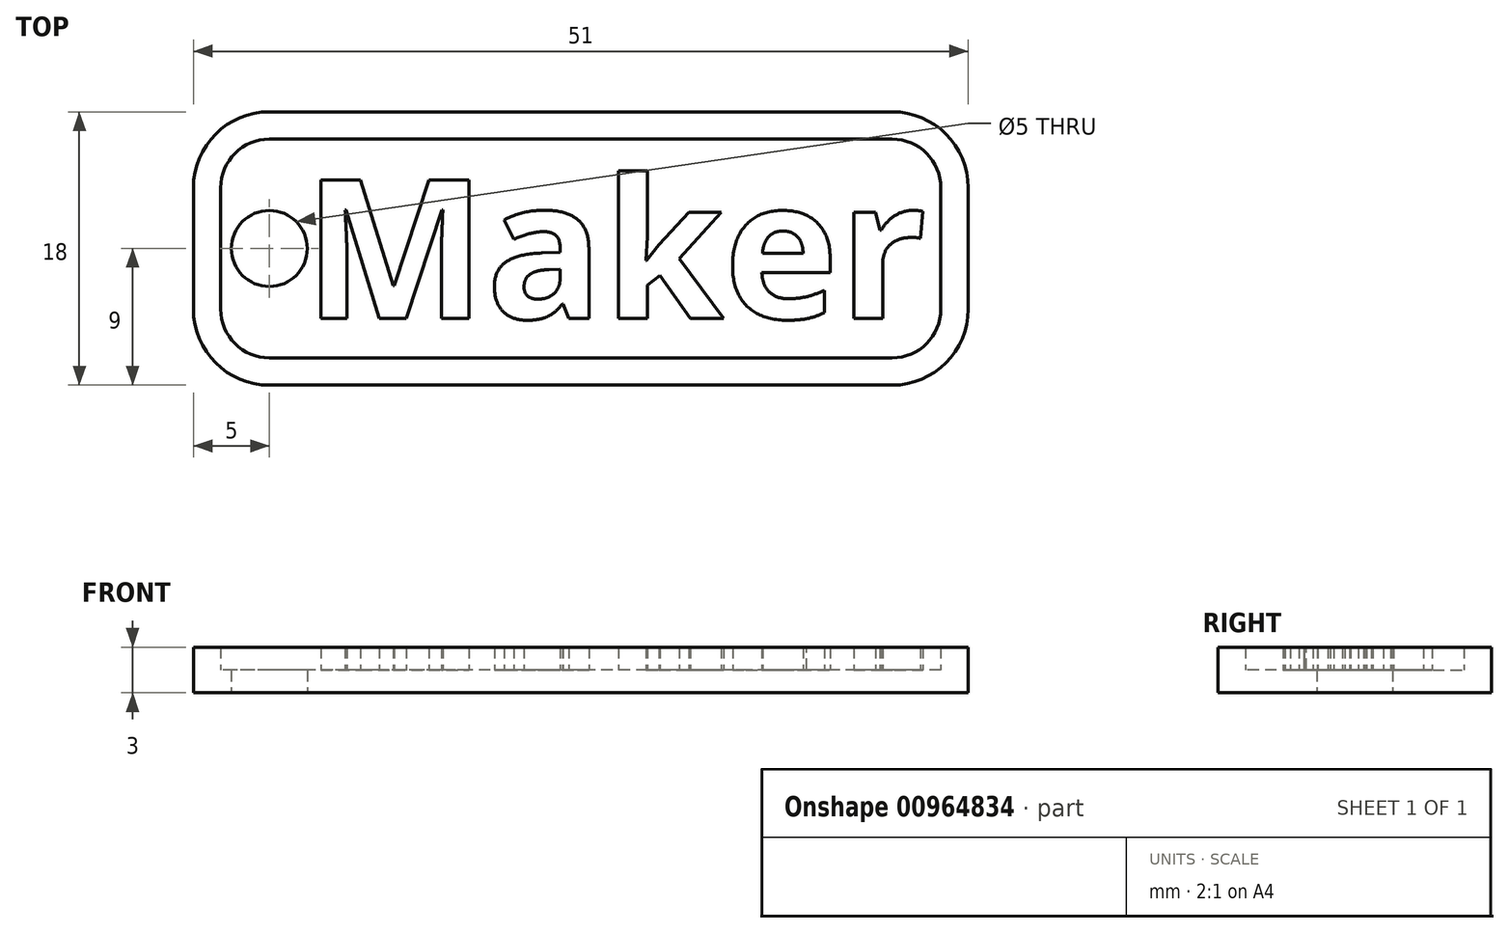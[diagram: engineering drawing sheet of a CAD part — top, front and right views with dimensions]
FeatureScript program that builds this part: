
annotation { "Feature Type Name" : "Feature", "Feature Type Description" : "" }
export const myFeature = defineFeature(function(context is Context, id is Id, definition is map)
    precondition{}
    {
        {
            var Q0;
            Q0=qCreatedBy(makeId("Top.planeOp"),FACE);
            var sketch = newSketch(context, id + "F0", { "sketchPlane" : qUnion([Q0])});
            skLineSegment(sketch, "E0.bottom", {"start": v(5, 0) * mm, "end": v(46, 0) * mm});
            skLineSegment(sketch, "E0.top", {"start": v(5, 18) * mm, "end": v(46, 18) * mm});
            skLineSegment(sketch, "E0.left", {"start": v(0, 5) * mm, "end": v(0, 13) * mm});
            skLineSegment(sketch, "E0.right", {"start": v(51, 5) * mm, "end": v(51, 13) * mm});
            skPoint(sketch, "E1.visualSharp", {"position": v(0, 18) * mm});
            skArc(sketch, "E1.filletArc", {"start": v(5, 18) * mm, "mid": v(1.46, 16.54) * mm, "end": v(0, 13) * mm});
            skPoint(sketch, "E2.visualSharp", {"position": v(0, 0) * mm});
            skArc(sketch, "E2.filletArc", {"start": v(0, 5) * mm, "mid": v(1.46, 1.46) * mm, "end": v(5, 0) * mm});
            skPoint(sketch, "E3.visualSharp", {"position": v(51, 0) * mm});
            skArc(sketch, "E3.filletArc", {"start": v(46, 0) * mm, "mid": v(49.54, 1.46) * mm, "end": v(51, 5) * mm});
            skPoint(sketch, "E4.visualSharp", {"position": v(51, 18) * mm});
            skArc(sketch, "E4.filletArc", {"start": v(51, 13) * mm, "mid": v(49.54, 16.54) * mm, "end": v(46, 18) * mm});
            skCircle(sketch, "E5", {"center": v(5, 9) * mm, "radius": 2.5 * mm});
            skSolve(sketch);
        }
        {
            var Q0;
            Q0=makeQuery(id+"F0.imprint","IMPRINT",FACE,{"disambiguationData":[TD([[makeQuery(id+"F0.imprint","IMPRINT",EDGE,{"derivedFrom":sQuery(id+"F0.wireOp",EDGE,"E0.bottom")}),1.0]])]});
            extrude(context, id + "F1", {"entities" : qUnion([Q0]), "depth" : 1.5 * mm, "offsetDistance" : 25 * mm});
        }
        {
            var Q0;
            Q0=makeQuery(id+"F1.opExtrude","CAP_FACE",FACE,{"disambiguationData":[OSD([sQuery(id+"F0.wireOp",EDGE,"E0.bottom"),sQuery(id+"F0.wireOp",EDGE,"E0.top"),sQuery(id+"F0.wireOp",EDGE,"E0.left"),sQuery(id+"F0.wireOp",EDGE,"E0.right"),sQuery(id+"F0.wireOp",EDGE,"E1.filletArc"),sQuery(id+"F0.wireOp",EDGE,"E2.filletArc"),sQuery(id+"F0.wireOp",EDGE,"E3.filletArc"),sQuery(id+"F0.wireOp",EDGE,"E4.filletArc"),sQuery(id+"F0.wireOp",EDGE,"E5")])],"isStart":false});
            var sketch = newSketch(context, id + "F2", { "sketchPlane" : qUnion([Q0])});
            skArc(sketch, "E6.0", {"start": v(49.2, 13) * mm, "mid": v(48.26, 15.26) * mm, "end": v(46, 16.2) * mm});
            skLineSegment(sketch, "E6.1", {"start": v(49.2, 5) * mm, "end": v(49.2, 13) * mm});
            skLineSegment(sketch, "E6.2", {"start": v(46, 16.2) * mm, "end": v(5, 16.2) * mm});
            skArc(sketch, "E6.3", {"start": v(46, 1.8) * mm, "mid": v(48.26, 2.74) * mm, "end": v(49.2, 5) * mm});
            skArc(sketch, "E6.4", {"start": v(5, 16.2) * mm, "mid": v(2.74, 15.26) * mm, "end": v(1.8, 13) * mm});
            skLineSegment(sketch, "E6.5", {"start": v(1.8, 13) * mm, "end": v(1.8, 5) * mm});
            skArc(sketch, "E6.6", {"start": v(1.8, 5) * mm, "mid": v(2.74, 2.74) * mm, "end": v(5, 1.8) * mm});
            skLineSegment(sketch, "E6.7", {"start": v(5, 1.8) * mm, "end": v(46, 1.8) * mm});
            skSolve(sketch);
        }
        {
            var Q0;
            Q0=makeQuery(id+"F2.imprint","IMPRINT",FACE,{"disambiguationData":[TD([[makeQuery(id+"F2.imprint","IMPRINT",EDGE,{"derivedFrom":sQuery(id+"F2.wireOp",EDGE,"E6.0")}),-1.0]])]});
            extrude(context, id + "F3", {"entities" : qUnion([Q0]), "operationType" : NewBodyOperationType.ADD, "depth" : 1.5 * mm, "offsetDistance" : 25 * mm});
        }
        {
            var Q0;
            Q0=makeQuery(id+"F1.opExtrude","CAP_FACE",FACE,{"disambiguationData":[OSD([sQuery(id+"F0.wireOp",EDGE,"E0.bottom"),sQuery(id+"F0.wireOp",EDGE,"E0.top"),sQuery(id+"F0.wireOp",EDGE,"E0.left"),sQuery(id+"F0.wireOp",EDGE,"E0.right"),sQuery(id+"F0.wireOp",EDGE,"E1.filletArc"),sQuery(id+"F0.wireOp",EDGE,"E2.filletArc"),sQuery(id+"F0.wireOp",EDGE,"E3.filletArc"),sQuery(id+"F0.wireOp",EDGE,"E4.filletArc"),sQuery(id+"F0.wireOp",EDGE,"E5")])],"isStart":false});
            var sketch = newSketch(context, id + "F4", { "sketchPlane" : qUnion([Q0])});
            skText(sketch, "E7", { "text": "Maker", "fontName": "OpenSans-Bold.ttf"});
            const initialGuessF4  = {"E7": [0.00723, 0.0044, 1, 0, 0.0092]};
            skSetInitialGuess(sketch, initialGuessF4);
            skSolve(sketch);
        }
        {
            var Q0;
            Q0 = qSketchRegion(id + "F4", true);
            extrude(context, id + "F5", {"entities" : qUnion([Q0]), "operationType" : NewBodyOperationType.ADD, "depth" : 1.5 * mm, "offsetDistance" : 25 * mm});
        }
    });
